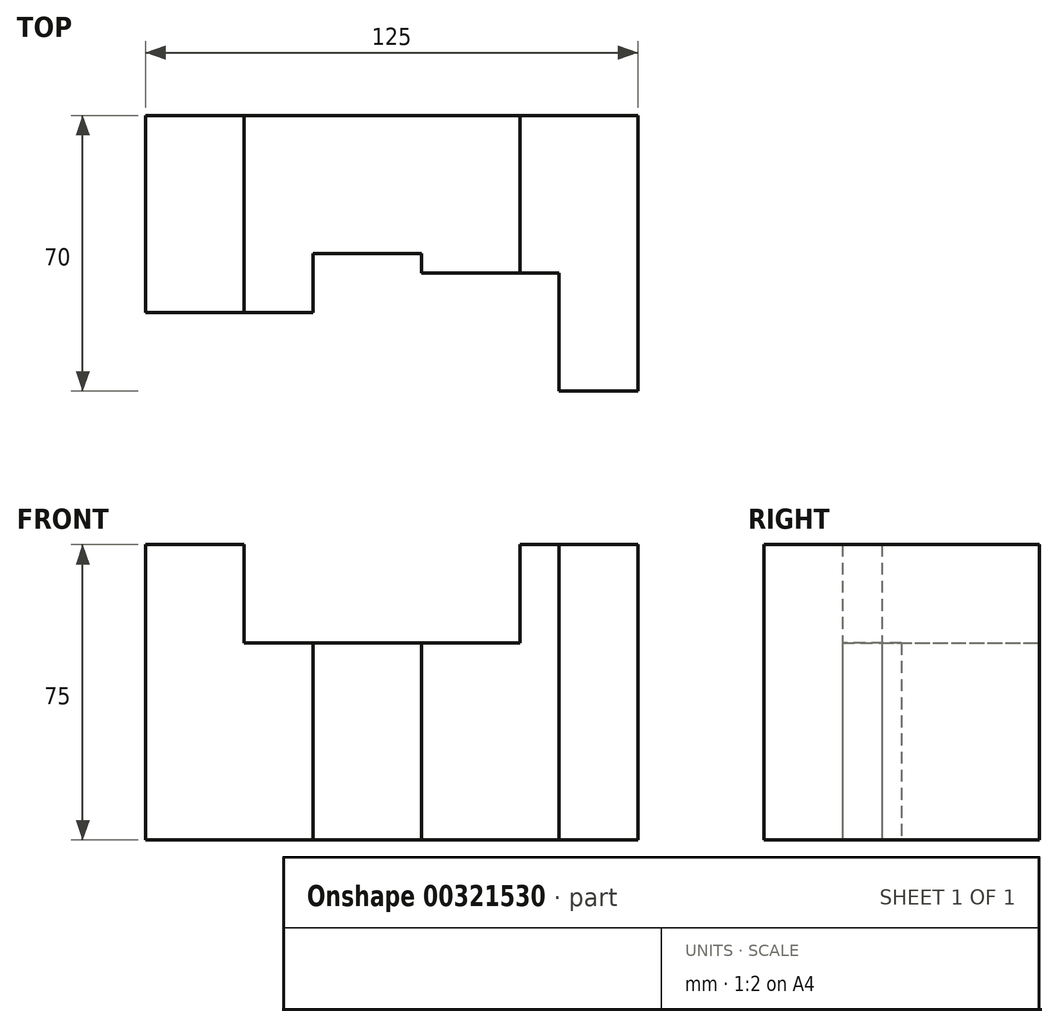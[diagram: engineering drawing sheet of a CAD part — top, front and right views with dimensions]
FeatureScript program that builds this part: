
annotation { "Feature Type Name" : "Feature", "Feature Type Description" : "" }
export const myFeature = defineFeature(function(context is Context, id is Id, definition is map)
    precondition{}
    {
        {
            var Q0;
            Q0=qCreatedBy(makeId("Top.planeOp"),FACE);
            var sketch = newSketch(context, id + "F0", { "sketchPlane" : qUnion([Q0])});
            skLineSegment(sketch, "E0", {"start": v(0, 0) * mm, "end": v(0, 50) * mm});
            skLineSegment(sketch, "E1", {"start": v(0, 50) * mm, "end": v(125, 50) * mm});
            skLineSegment(sketch, "E2", {"start": v(125, 50) * mm, "end": v(125, -20) * mm});
            skLineSegment(sketch, "E3", {"start": v(125, -20) * mm, "end": v(105, -20) * mm});
            skLineSegment(sketch, "E4", {"start": v(105, -20) * mm, "end": v(105, 10) * mm});
            skLineSegment(sketch, "E5", {"start": v(105, 10) * mm, "end": v(70, 10) * mm});
            skLineSegment(sketch, "E6", {"start": v(70, 10) * mm, "end": v(70, 15) * mm});
            skLineSegment(sketch, "E7", {"start": v(70, 15) * mm, "end": v(42.5, 15) * mm});
            skLineSegment(sketch, "E8", {"start": v(42.5, 15) * mm, "end": v(42.5, 0) * mm});
            skLineSegment(sketch, "E9", {"start": v(42.5, 0) * mm, "end": v(0, 0) * mm});
            skLineSegment(sketch, "E10", {"start": v(25, 0) * mm, "end": v(25, 50) * mm});
            skLineSegment(sketch, "E11", {"start": v(95, 10) * mm, "end": v(95, 50) * mm});
            skSolve(sketch);
        }
        {
            var Q0;
            {var subQ0=sQuery(id+"F0.wireOp",EDGE,"E6");Q0=makeQuery(id+"F0.imprint","IMPRINT",FACE,{"disambiguationData":[TD([[makeQuery(id+"F0.imprint","IMPRINT",EDGE,{"derivedFrom":subQ0}),-1.0]])]});}
            extrude(context, id + "F1", {"entities" : qUnion([Q0]), "depth" : 50 * mm});
        }
        {
            var Q0;
            {var subQ0=sQuery(id+"F0.wireOp",EDGE,"E0");Q0=makeQuery(id+"F0.imprint","IMPRINT",FACE,{"disambiguationData":[TD([[makeQuery(id+"F0.imprint","IMPRINT",EDGE,{"derivedFrom":subQ0}),-1.0]])]});}
            var Q1;
            {var subQ1=sQuery(id+"F0.wireOp",EDGE,"E2");Q1=makeQuery(id+"F0.imprint","IMPRINT",FACE,{"disambiguationData":[TD([[makeQuery(id+"F0.imprint","IMPRINT",EDGE,{"derivedFrom":subQ1}),-1.0]])]});}
            extrude(context, id + "F2", {"entities" : qUnion([Q0, Q1]), "operationType" : NewBodyOperationType.ADD, "depth" : (15 * 5) * mm});
        }
    });
